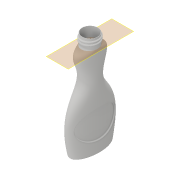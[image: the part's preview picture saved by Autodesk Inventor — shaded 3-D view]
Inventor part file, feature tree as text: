
AUTODESK INVENTOR PART (.ipt)
format: ipt  version: 2017 (Build 210142000, 142)  size: 1,437,696 bytes
history: native  units: in
note: dims shown in document units (in); Inventor stores cm internally (conversion verified against a paired STEP export)
features: sketch x8, plane x2, revolve x2, loft x1, extrude x1, emboss x1, mirror x1, fillet x1, shell x1, helix x1
ambient origin geometry x8: Origin, YZ Plane, XZ Plane, XY Plane, X Axis, Y Axis, Z Axis, Center Point
bodies: Solid1 (feature_tree)
feature tree (19):
  sketch  "Sketch1"  dims[d2=1.968in d3=0.984in]
  sketch  "Sketch2"  dims[d4=1.968in d5=2.362in d6=2.165in d7=1.575in d8=0.984in]
  plane  "Work Plane1"
  loft  "Loft1"
  extrude  "Extrusion1"  Depth=2.362in
  plane  "Work Plane2"
  emboss  "Emboss1"
  mirror  "Mirror1"
  fillet  "Fillet1"  Radius=2.165in
  shell  "Shell1"  Thickness=1.575in
  helix  "Coil1"  [1 undecoded]
  revolve  "Revolution1"  [1 undecoded]
  revolve  "Revolution2"  [1 undecoded]
  sketch  "Sketch4"  dims[d9=1.378in d10=0.787in]
  sketch  "Sketch5"  dims[d11=8.858in d12=7.677in]
  sketch  "Sketch6"  dims[d13=6.102in]
  sketch  "Sketch7"  dims[d14=4.921in]
  sketch  "Sketch8"  dims[d15=3.74in]
  sketch  "Sketch9"  dims[d16=2.362in d17=8.858in d18=1.574in d19=0.0in d20=90.0deg d21=0.0in d22=90.0deg d23=0.0in d24=90.0deg d25=0.0in d26=90.0deg d27=1.574in d28=1.0in d29=0.0in d30=2.0in d31=2.0in d32=1.35in d33=2.55in d34=0.125in d35=0.0in d36=0.2in d37=0.04in d38=0.03in d40=60.0deg d41=1.516in d42=0.125in d43=0.22in d44=9.65in d45=0.04in d46=0.275in d47=1.0in d48=0.7874in d49=0.0in d50=90.0deg d51=90.0deg d52=0.0in d53=0.0in d54=0.6871in d55=0.6871in]
note: 3 required parameter values undecoded (feature->parameter linkage not recoverable at this tier; creation-order binding heuristic only, values carry confidence <= 0.55)